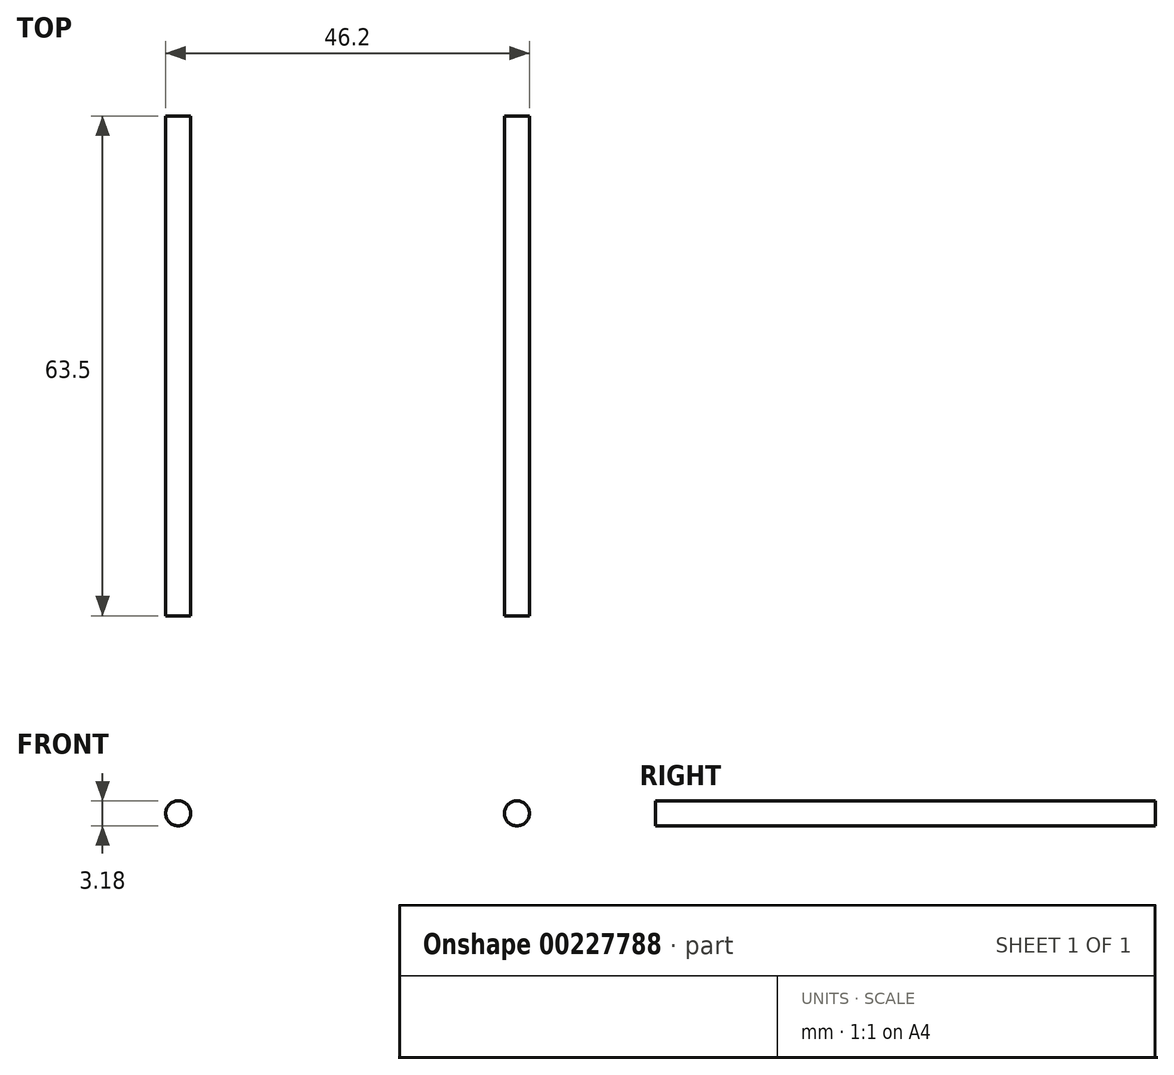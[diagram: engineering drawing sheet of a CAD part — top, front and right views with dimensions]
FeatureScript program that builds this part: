
annotation { "Feature Type Name" : "Feature", "Feature Type Description" : "" }
export const myFeature = defineFeature(function(context is Context, id is Id, definition is map)
    precondition{}
    {
        {
            var Q0;
            Q0=qCreatedBy(makeId("Front.planeOp"),FACE);
            var sketch = newSketch(context, id + "F0", { "sketchPlane" : qUnion([Q0])});
            skCircle(sketch, "E0", {"center": v(-24.17, 0) * mm, "radius": 1.59 * mm});
            skCircle(sketch, "E1", {"center": v(18.85, 0) * mm, "radius": 1.59 * mm});
            skSolve(sketch);
        }
        {
            var Q0;
            Q0=qSketchRegion(id+"F0",true);
            extrude(context, id + "F1", {"entities" : qUnion([Q0]), "depth" : 38.1 * mm});
        }
        {
            var Q0;
            Q0=makeQuery(id+"F1.opExtrude","CAP_FACE",FACE,{"disambiguationData":[OSD([sQuery(id+"F0.wireOp",EDGE,"E1")])],"isStart":false});
            extrude(context, id + "F2", {"entities" : qUnion([Q0]), "operationType" : NewBodyOperationType.ADD, "depth" : 25.4 * mm});
        }
        {
            var Q0;
            Q0=makeQuery(id+"F1.opExtrude","CAP_FACE",FACE,{"disambiguationData":[OSD([sQuery(id+"F0.wireOp",EDGE,"E0")])],"isStart":false});
            extrude(context, id + "F3", {"entities" : qUnion([Q0]), "operationType" : NewBodyOperationType.ADD, "depth" : 25.4 * mm});
        }
    });
